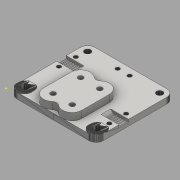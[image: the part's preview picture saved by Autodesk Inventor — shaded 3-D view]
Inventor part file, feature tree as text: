
AUTODESK INVENTOR PART (.ipt)
format: ipt  version: 2016 (Build 200138000, 138)  size: 1,937,408 bytes
history: native  units: mm
features: sketch x5, extrude x4, other x2, plane x1, mirror x1, fillet x1
ambient origin geometry x8: Origin, YZ Plane, XZ Plane, XY Plane, X Axis, Y Axis, Z Axis, Center Point
bodies: Solid1 (feature_tree)
feature tree (14):
  other  "1-Print_Carriage_Front"
  other  "MeshFeature1"
  extrude  "Extrusion1"  Depth=10.0mm
  extrude  "Extrusion2"  Depth=8.0mm
  extrude  "Extrusion3"  Depth=4.2mm
  extrude  "Extrusion4"  Depth=6.0mm TaperAngle=0.0deg
  sketch  "Sketch5"  dims[d12=8.0mm d13=4.0mm d14=0.0mm d15=4.0mm]
  plane  "Work Plane1"
  mirror  "Mirror1"
  fillet  "Fillet1"  Radius=8.0mm
  sketch  "Sketch1"  dims[d0=10.0mm d1=0.0mm d2=23.0mm]
  sketch  "Sketch2"  dims[d3=8.0mm d4=8.0mm]
  sketch  "Sketch3"  dims[d5=4.2mm d6=4.2mm]
  sketch  "Sketch4"  dims[d7=10.0mm d8=0.0mm d9=6.0mm d10=0.0mm d11=8.0mm]
